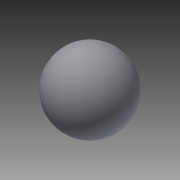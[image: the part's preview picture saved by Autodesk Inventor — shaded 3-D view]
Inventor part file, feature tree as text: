
AUTODESK INVENTOR PART (.ipt)
format: ipt  version: 2015 (Build 190159000, 159)  size: 101,888 bytes
history: native  units: in
note: dims shown in document units (in); Inventor stores cm internally (conversion verified against a paired STEP export)
features: revolve x1, sketch x1
ambient origin geometry x8: Origin, YZ Plane, XZ Plane, XY Plane, X Axis, Y Axis, Z Axis, Center Point
bodies: Solid1 (feature_tree)
feature tree (2):
  revolve  "Revolution1"  Angle=90.0deg
  sketch  "Sketch1"  dims[d0=0.2in d1=90.0deg]
